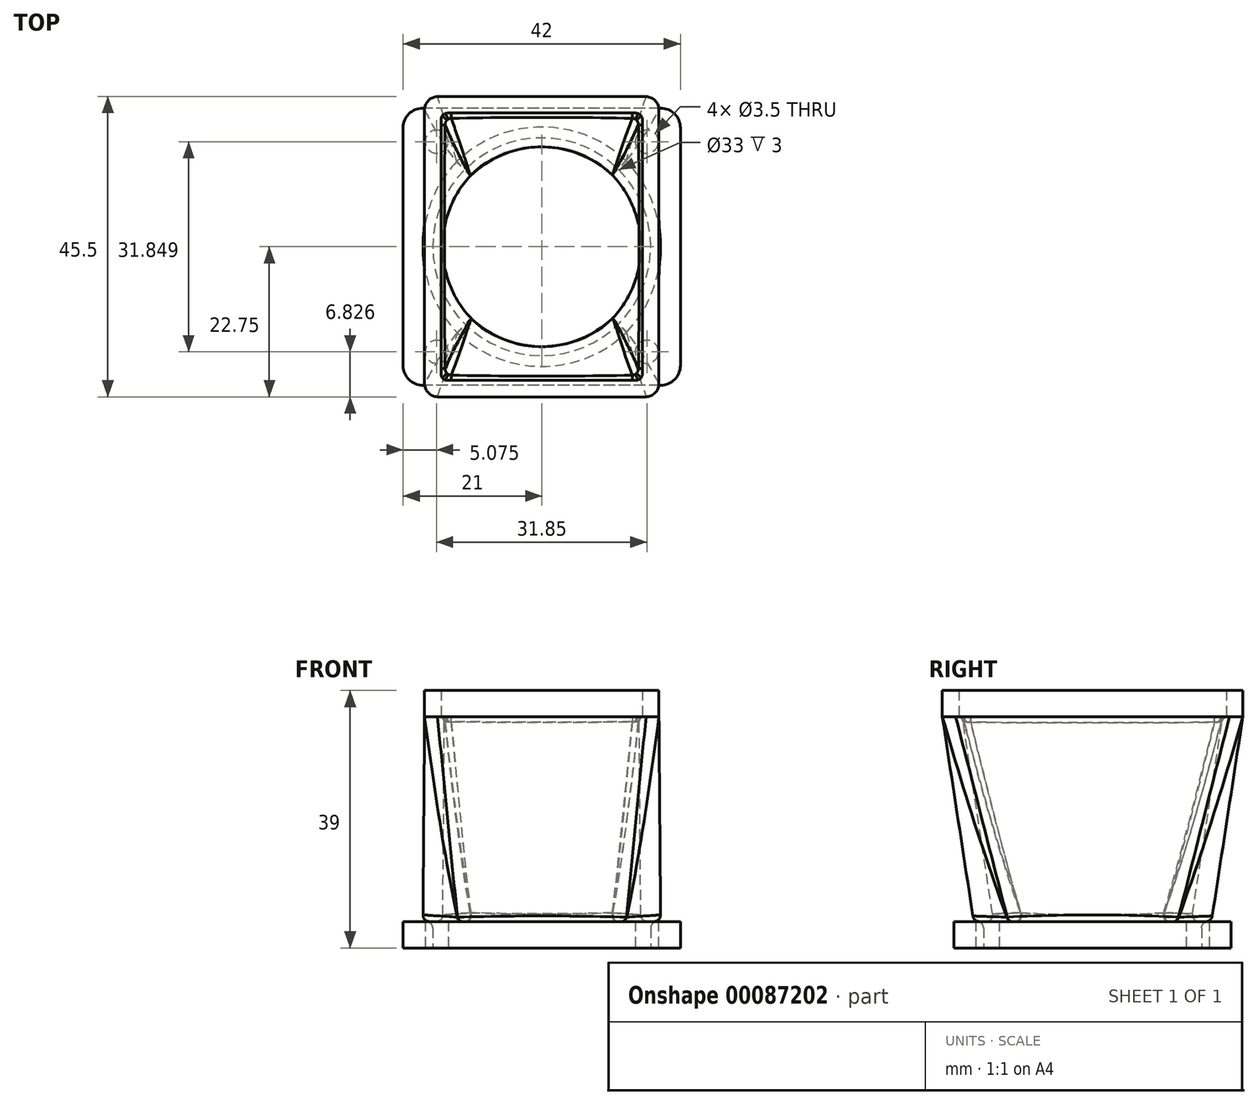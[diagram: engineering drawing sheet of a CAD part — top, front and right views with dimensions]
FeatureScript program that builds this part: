
annotation { "Feature Type Name" : "Feature", "Feature Type Description" : "" }
export const myFeature = defineFeature(function(context is Context, id is Id, definition is map)
    precondition{}
    {
        {
            var Q0;
            Q0=qCreatedBy(makeId("Top.planeOp"),FACE);
            var sketch = newSketch(context, id + "F0", { "sketchPlane" : qUnion([Q0])});
            skLineSegment(sketch, "E0.bottom", {"start": v(21, 21) * mm, "end": v(-21, 21) * mm});
            skLineSegment(sketch, "E0.top", {"start": v(21, -21) * mm, "end": v(-21, -21) * mm});
            skLineSegment(sketch, "E0.left", {"start": v(21, 21) * mm, "end": v(21, -21) * mm});
            skLineSegment(sketch, "E0.right", {"start": v(-21, 21) * mm, "end": v(-21, -21) * mm});
            skPoint(sketch, "E0.middle", {"position": v(0, 0) * mm});
            skCircle(sketch, "E1", {"center": v(15.93, 15.92) * mm, "radius": 1.75 * mm});
            skCircle(sketch, "E2", {"center": v(15.93, -15.92) * mm, "radius": 1.75 * mm});
            skCircle(sketch, "E3", {"center": v(-15.92, -15.92) * mm, "radius": 1.75 * mm});
            skCircle(sketch, "E4", {"center": v(-15.93, 15.92) * mm, "radius": 1.75 * mm});
            skLineSegment(sketch, "E5", {"start": v(-17.68, 23.33) * mm, "end": v(-17.68, 11.4) * mm, "construction": true});
            skLineSegment(sketch, "E6", {"start": v(17.67, 22.53) * mm, "end": v(17.67, 11.7) * mm, "construction": true});
            skLineSegment(sketch, "E7", {"start": v(0, 27.98) * mm, "end": v(0, -28.6) * mm, "construction": true});
            skLineSegment(sketch, "E8", {"start": v(-15.93, 15.92) * mm, "end": v(0, 15.92) * mm, "construction": true});
            skLineSegment(sketch, "E9", {"start": v(0, 15.92) * mm, "end": v(15.93, 15.92) * mm, "construction": true});
            skLineSegment(sketch, "E10", {"start": v(-15.93, 15.92) * mm, "end": v(-15.93, 0) * mm, "construction": true});
            skLineSegment(sketch, "E11", {"start": v(-15.93, 0) * mm, "end": v(-15.92, -15.92) * mm, "construction": true});
            skLineSegment(sketch, "E12", {"start": v(-21.25, 17.67) * mm, "end": v(-8.97, 17.67) * mm, "construction": true});
            skLineSegment(sketch, "E13", {"start": v(-20.93, -17.67) * mm, "end": v(-10.43, -17.67) * mm, "construction": true});
            skCircle(sketch, "E14", {"center": v(0, 0) * mm, "radius": 16.5 * mm});
            skSolve(sketch);
        }
        {
            var Q0;
            Q0=makeQuery(id+"F0.imprint","IMPRINT",FACE,{"disambiguationData":[TD([[makeQuery(id+"F0.imprint","IMPRINT",EDGE,{"derivedFrom":sQuery(id+"F0.wireOp",EDGE,"E0.bottom")}),1.0]])]});
            extrude(context, id + "F1", {"entities" : qUnion([Q0]), "depth" : 4 * mm});
        }
        {
            var Q0;
            Q0=qCreatedBy(makeId("Top.planeOp"),FACE);
            cPlane(context, id + "F2", {"entities" : qUnion([Q0]), "cplaneType" : CPlaneType.OFFSET, "offset" : 35 * mm, "width" : 150 * mm, "height" : 150 * mm});
        }
        {
            var Q0;
            Q0=qCreatedBy(id+"F2.planeOp",FACE);
            var sketch = newSketch(context, id + "F3", { "sketchPlane" : qUnion([Q0])});
            skPoint(sketch, "E15.middle", {"position": v(0, 0) * mm});
            skLineSegment(sketch, "E16.0", {"start": v(17.75, 22.75) * mm, "end": v(-17.75, 22.75) * mm});
            skLineSegment(sketch, "E16.1", {"start": v(17.75, -22.75) * mm, "end": v(17.75, 22.75) * mm});
            skLineSegment(sketch, "E16.2", {"start": v(17.75, -22.75) * mm, "end": v(-17.75, -22.75) * mm});
            skLineSegment(sketch, "E16.3", {"start": v(-17.75, -22.75) * mm, "end": v(-17.75, 22.75) * mm});
            skSolve(sketch);
        }
        {
            var Q0;
            Q0=qCreatedBy(makeId("Top.planeOp"),FACE);
            cPlane(context, id + "F4", {"entities" : qUnion([Q0]), "cplaneType" : CPlaneType.OFFSET, "offset" : 4 * mm, "width" : 150 * mm, "height" : 150 * mm});
        }
        {
            var Q0;
            Q0=qCreatedBy(id+"F4.planeOp",FACE);
            var sketch = newSketch(context, id + "F5", { "sketchPlane" : qUnion([Q0])});
            skLineSegment(sketch, "E17", {"start": v(-12.73, -12.73) * mm, "end": v(-12.73, -12.73) * mm});
            skLineSegment(sketch, "E18", {"start": v(-12.73, 12.73) * mm, "end": v(-12.73, 12.73) * mm});
            skLineSegment(sketch, "E19", {"start": v(12.73, 12.73) * mm, "end": v(12.73, 12.73) * mm});
            skLineSegment(sketch, "E20", {"start": v(12.7, -12.7) * mm, "end": v(12.73, -12.73) * mm, "construction": true});
            skArc(sketch, "E21", {"start": v(-12.79, 12.67) * mm, "mid": v(-18, -0.1) * mm, "end": v(-12.66, -12.8) * mm});
            skArc(sketch, "E22", {"start": v(-12.66, -12.8) * mm, "mid": v(0.05, -18) * mm, "end": v(12.73, -12.73) * mm});
            skArc(sketch, "E23", {"start": v(12.73, -12.73) * mm, "mid": v(18, 0.05) * mm, "end": v(12.65, 12.8) * mm});
            skArc(sketch, "E24", {"start": v(12.65, 12.8) * mm, "mid": v(-0.1, 18) * mm, "end": v(-12.79, 12.67) * mm});
            skSolve(sketch);
        }
        {
            var Q0;
            Q0=makeQuery(id+"F5.imprint","IMPRINT",FACE,{"disambiguationData":[TD([[makeQuery(id+"F5.imprint","IMPRINT",EDGE,{"derivedFrom":sQuery(id+"F5.wireOp",EDGE,"E21")}),1.0]])]});
            var Q1;
            Q1=makeQuery(id+"F3.imprint","IMPRINT",FACE,{"disambiguationData":[TD([[makeQuery(id+"F3.imprint","IMPRINT",EDGE,{"derivedFrom":sQuery(id+"F3.wireOp",EDGE,"E16.0")}),1.0]])]});
            loft(context, id + "F6", {"sheetProfilesArray" : [{ "sheetProfileEntities" : qUnion([Q0]) }, { "sheetProfileEntities" : qUnion([Q1]) }]});
        }
        {
            var Q0;
            Q0=makeQuery(id+"F6.opLoft","CAP_FACE",FACE,{"disambiguationData":[OSD([makeQuery(id+"F3.imprint","IMPRINT",FACE,{"disambiguationData":[TD([[makeQuery(id+"F3.imprint","IMPRINT",EDGE,{"derivedFrom":sQuery(id+"F3.wireOp",EDGE,"E16.0")}),1.0]])]})])],"isStart":true});
            var Q1;
            Q1=makeQuery(id+"F6.opLoft","CAP_FACE",FACE,{"disambiguationData":[OSD([makeQuery(id+"F5.imprint","IMPRINT",FACE,{"disambiguationData":[TD([[makeQuery(id+"F5.imprint","IMPRINT",EDGE,{"derivedFrom":sQuery(id+"F5.wireOp",EDGE,"E21")}),1.0]])]})])],"isStart":true});
            var Q2;
            Q2=makeQuery(id+"F6.opLoft","SWEPT_BODY",BODY,{"disambiguationData":[OSD([makeQuery(id+"F3.imprint","IMPRINT",FACE,{"disambiguationData":[TD([[makeQuery(id+"F3.imprint","IMPRINT",EDGE,{"derivedFrom":sQuery(id+"F3.wireOp",EDGE,"E16.0")}),1.0]])]}),makeQuery(id+"F5.imprint","IMPRINT",FACE,{"disambiguationData":[TD([[makeQuery(id+"F5.imprint","IMPRINT",EDGE,{"derivedFrom":sQuery(id+"F5.wireOp",EDGE,"E21")}),1.0]])]})])]});
            shell(context, id + "F7", {"entities" : qUnion([Q0, Q1]), "parts" : qUnion([Q2]), "thickness" : 3 * mm});
        }
        {
            var Q0;
            Q0=makeQuery(id+"F7.opShell","OFFSET_EDGE",EDGE,{"disambiguationData":[OSD([sQuery(id+"F3.wireOp",EDGE,"E16.2"),sQuery(id+"F3.wireOp",EDGE,"E16.3"),sQuery(id+"F5.wireOp",EDGE,"E21"),sQuery(id+"F5.wireOp",EDGE,"E22")])]});
            var Q1;
            Q1=makeQuery(id+"F7.opShell","OFFSET_EDGE",EDGE,{"disambiguationData":[OSD([sQuery(id+"F3.wireOp",EDGE,"E16.1"),sQuery(id+"F3.wireOp",EDGE,"E16.2"),sQuery(id+"F5.wireOp",EDGE,"E22"),sQuery(id+"F5.wireOp",EDGE,"E23")])]});
            var Q2;
            Q2=makeQuery(id+"F7.opShell","OFFSET_EDGE",EDGE,{"disambiguationData":[OSD([sQuery(id+"F3.wireOp",EDGE,"E16.0"),sQuery(id+"F3.wireOp",EDGE,"E16.1"),sQuery(id+"F5.wireOp",EDGE,"E23"),sQuery(id+"F5.wireOp",EDGE,"E24")])]});
            var Q3;
            Q3=makeQuery(id+"F7.opShell","OFFSET_EDGE",EDGE,{"disambiguationData":[OSD([sQuery(id+"F3.wireOp",EDGE,"E16.0"),sQuery(id+"F3.wireOp",EDGE,"E16.3"),sQuery(id+"F5.wireOp",EDGE,"E21"),sQuery(id+"F5.wireOp",EDGE,"E24")])]});
            fillet(context, id + "F8", {"entities" : qUnion([Q0, Q1, Q2, Q3]), "radius" : 1 * mm, "tangentPropagation" : true, "allowEdgeOverflow" : false});
        }
        {
            var Q0;
            Q0=makeQuery(id+"F6.opLoft","SWEPT_EDGE",EDGE,{"disambiguationData":[OSD([sQuery(id+"F3.wireOp",EDGE,"E16.2"),sQuery(id+"F3.wireOp",EDGE,"E16.3"),sQuery(id+"F5.wireOp",EDGE,"E21"),sQuery(id+"F5.wireOp",EDGE,"E22")])]});
            var Q1;
            Q1=makeQuery(id+"F6.opLoft","SWEPT_EDGE",EDGE,{"disambiguationData":[OSD([sQuery(id+"F3.wireOp",EDGE,"E16.0"),sQuery(id+"F3.wireOp",EDGE,"E16.3"),sQuery(id+"F5.wireOp",EDGE,"E21"),sQuery(id+"F5.wireOp",EDGE,"E24")])]});
            var Q2;
            Q2=makeQuery(id+"F6.opLoft","SWEPT_EDGE",EDGE,{"disambiguationData":[OSD([sQuery(id+"F3.wireOp",EDGE,"E16.0"),sQuery(id+"F3.wireOp",EDGE,"E16.1"),sQuery(id+"F5.wireOp",EDGE,"E23"),sQuery(id+"F5.wireOp",EDGE,"E24")])]});
            var Q3;
            Q3=makeQuery(id+"F6.opLoft","SWEPT_EDGE",EDGE,{"disambiguationData":[OSD([sQuery(id+"F3.wireOp",EDGE,"E16.1"),sQuery(id+"F3.wireOp",EDGE,"E16.2"),sQuery(id+"F5.wireOp",EDGE,"E22"),sQuery(id+"F5.wireOp",EDGE,"E23")])]});
            fillet(context, id + "F9", {"entities" : qUnion([Q0, Q1, Q2, Q3]), "radius" : 2 * mm, "tangentPropagation" : true, "allowEdgeOverflow" : false});
        }
        {
            var Q0;
            Q0=makeQuery(id+"F6.opLoft","MID_CAP_EDGE",EDGE,{"disambiguationData":[OSD([sQuery(id+"F5.wireOp",EDGE,"E21"),sQuery(id+"F5.wireOp",EDGE,"E22"),sQuery(id+"F5.wireOp",EDGE,"E24")])],"capPos":0.0});
            var Q1;
            Q1=makeQuery(id+"F6.opLoft","MID_CAP_EDGE",EDGE,{"disambiguationData":[OSD([sQuery(id+"F5.wireOp",EDGE,"E21"),sQuery(id+"F5.wireOp",EDGE,"E23"),sQuery(id+"F5.wireOp",EDGE,"E24")])],"capPos":0.0});
            var Q2;
            Q2=makeQuery(id+"F6.opLoft","MID_CAP_EDGE",EDGE,{"disambiguationData":[OSD([sQuery(id+"F5.wireOp",EDGE,"E21"),sQuery(id+"F5.wireOp",EDGE,"E22"),sQuery(id+"F5.wireOp",EDGE,"E23")])],"capPos":0.0});
            var Q3;
            Q3=makeQuery(id+"F6.opLoft","MID_CAP_EDGE",EDGE,{"disambiguationData":[OSD([sQuery(id+"F5.wireOp",EDGE,"E22"),sQuery(id+"F5.wireOp",EDGE,"E23"),sQuery(id+"F5.wireOp",EDGE,"E24")])],"capPos":0.0});
            fillet(context, id + "F10", {"entities" : qUnion([Q0, Q1, Q2, Q3]), "radius" : 1 * mm, "tangentPropagation" : true, "allowEdgeOverflow" : false});
        }
        {
            var Q0;
            Q0=makeQuery(id+"F3.imprint","IMPRINT",FACE,{"disambiguationData":[TD([[makeQuery(id+"F3.imprint","IMPRINT",EDGE,{"derivedFrom":sQuery(id+"F3.wireOp",EDGE,"E16.0")}),1.0]])]});
            var sketch = newSketch(context, id + "F11", { "sketchPlane" : qUnion([Q0])});
            skLineSegment(sketch, "E25.bottom", {"start": v(-15.25, 20.25) * mm, "end": v(15.25, 20.25) * mm});
            skLineSegment(sketch, "E25.top", {"start": v(-15.25, -20.25) * mm, "end": v(15.25, -20.25) * mm});
            skLineSegment(sketch, "E25.left", {"start": v(-15.25, 20.25) * mm, "end": v(-15.25, -20.25) * mm});
            skLineSegment(sketch, "E25.right", {"start": v(15.25, 20.25) * mm, "end": v(15.25, -20.25) * mm});
            skPoint(sketch, "E25.middle", {"position": v(0, 0) * mm});
            skLineSegment(sketch, "E26.0", {"start": v(-15.75, -22.75) * mm, "end": v(15.75, -22.75) * mm});
            skLineSegment(sketch, "E26.1", {"start": v(-17.75, 20.75) * mm, "end": v(-17.75, -20.75) * mm});
            skLineSegment(sketch, "E26.2", {"start": v(-15.75, 22.75) * mm, "end": v(15.75, 22.75) * mm});
            skLineSegment(sketch, "E26.3", {"start": v(17.75, 20.75) * mm, "end": v(17.75, -20.75) * mm});
            skPoint(sketch, "E27.visualSharp", {"position": v(-17.75, 22.75) * mm});
            skArc(sketch, "E27.filletArc", {"start": v(-15.75, 22.75) * mm, "mid": v(-17.16, 22.16) * mm, "end": v(-17.75, 20.75) * mm});
            skPoint(sketch, "E28.visualSharp", {"position": v(17.75, 22.75) * mm});
            skArc(sketch, "E28.filletArc", {"start": v(17.75, 20.75) * mm, "mid": v(17.16, 22.16) * mm, "end": v(15.75, 22.75) * mm});
            skPoint(sketch, "E29.visualSharp", {"position": v(-17.75, -22.75) * mm});
            skArc(sketch, "E29.filletArc", {"start": v(-17.75, -20.75) * mm, "mid": v(-17.16, -22.16) * mm, "end": v(-15.75, -22.75) * mm});
            skPoint(sketch, "E30.visualSharp", {"position": v(17.75, -22.75) * mm});
            skArc(sketch, "E30.filletArc", {"start": v(15.75, -22.75) * mm, "mid": v(17.16, -22.16) * mm, "end": v(17.75, -20.75) * mm});
            skSolve(sketch);
        }
        {
            var Q0;
            Q0=makeQuery(id+"F1.opExtrude","SWEPT_EDGE",EDGE,{"disambiguationData":[OSD([sQuery(id+"F0.wireOp",EDGE,"E0.top"),sQuery(id+"F0.wireOp",EDGE,"E0.left")])]});
            var Q1;
            Q1=makeQuery(id+"F1.opExtrude","SWEPT_EDGE",EDGE,{"disambiguationData":[OSD([sQuery(id+"F0.wireOp",EDGE,"E0.top"),sQuery(id+"F0.wireOp",EDGE,"E0.right")])]});
            var Q2;
            Q2=makeQuery(id+"F1.opExtrude","SWEPT_EDGE",EDGE,{"disambiguationData":[OSD([sQuery(id+"F0.wireOp",EDGE,"E0.bottom"),sQuery(id+"F0.wireOp",EDGE,"E0.right")])]});
            var Q3;
            Q3=makeQuery(id+"F1.opExtrude","SWEPT_EDGE",EDGE,{"disambiguationData":[OSD([sQuery(id+"F0.wireOp",EDGE,"E0.bottom"),sQuery(id+"F0.wireOp",EDGE,"E0.left")])]});
            fillet(context, id + "F12", {"entities" : qUnion([Q0, Q1, Q2, Q3]), "radius" : 3 * mm, "tangentPropagation" : true, "allowEdgeOverflow" : false});
        }
        {
            var Q0;
            Q0 = qSketchRegion(id + "F11", true);
            extrude(context, id + "F13", {"entities" : qUnion([Q0]), "operationType" : NewBodyOperationType.ADD, "depth" : 4 * mm});
        }
        {
            var Q0;
            Q0=makeQuery(id+"F13.opExtrude","SWEPT_EDGE",EDGE,{"disambiguationData":[OSD([sQuery(id+"F11.wireOp",EDGE,"E25.top"),sQuery(id+"F11.wireOp",EDGE,"E25.right")])]});
            var Q1;
            Q1=makeQuery(id+"F13.opExtrude","SWEPT_EDGE",EDGE,{"disambiguationData":[OSD([sQuery(id+"F11.wireOp",EDGE,"E25.bottom"),sQuery(id+"F11.wireOp",EDGE,"E25.right")])]});
            var Q2;
            Q2=makeQuery(id+"F13.opExtrude","SWEPT_EDGE",EDGE,{"disambiguationData":[OSD([sQuery(id+"F11.wireOp",EDGE,"E25.top"),sQuery(id+"F11.wireOp",EDGE,"E25.left")])]});
            var Q3;
            Q3=makeQuery(id+"F13.opExtrude","SWEPT_EDGE",EDGE,{"disambiguationData":[OSD([sQuery(id+"F11.wireOp",EDGE,"E25.bottom"),sQuery(id+"F11.wireOp",EDGE,"E25.left")])]});
            fillet(context, id + "F14", {"entities" : qUnion([Q0, Q1, Q2, Q3]), "radius" : 1 * mm, "tangentPropagation" : true, "allowEdgeOverflow" : false});
        }
        {
            var Q0;
            Q0=makeQuery(id+"F1.opExtrude","CAP_EDGE",EDGE,{"disambiguationData":[OSD([sQuery(id+"F0.wireOp",EDGE,"E14")])],"isStart":false});
            fillet(context, id + "F15", {"entities" : qUnion([Q0]), "radius" : 1 * mm, "tangentPropagation" : true, "allowEdgeOverflow" : false});
        }
        {
            var Q0;
            Q0=makeQuery(id+"F7.opShell","OFFSET_EDGE",EDGE,{"disambiguationData":[OSD([sQuery(id+"F5.wireOp",EDGE,"E22"),sQuery(id+"F5.wireOp",EDGE,"E23"),sQuery(id+"F5.wireOp",EDGE,"E24")])]});
            var Q1;
            Q1=makeQuery(id+"F7.opShell","OFFSET_FACE",FACE,{"disambiguationData":[OSD([sQuery(id+"F3.wireOp",EDGE,"E16.1"),sQuery(id+"F3.wireOp",EDGE,"E16.2"),sQuery(id+"F3.wireOp",EDGE,"E16.3"),sQuery(id+"F5.wireOp",EDGE,"E21"),sQuery(id+"F5.wireOp",EDGE,"E22"),sQuery(id+"F5.wireOp",EDGE,"E23")])]});
            fillet(context, id + "F16", {"entities" : qUnion([Q0, Q1]), "radius" : 1 * mm, "tangentPropagation" : true, "allowEdgeOverflow" : false});
        }
    });
